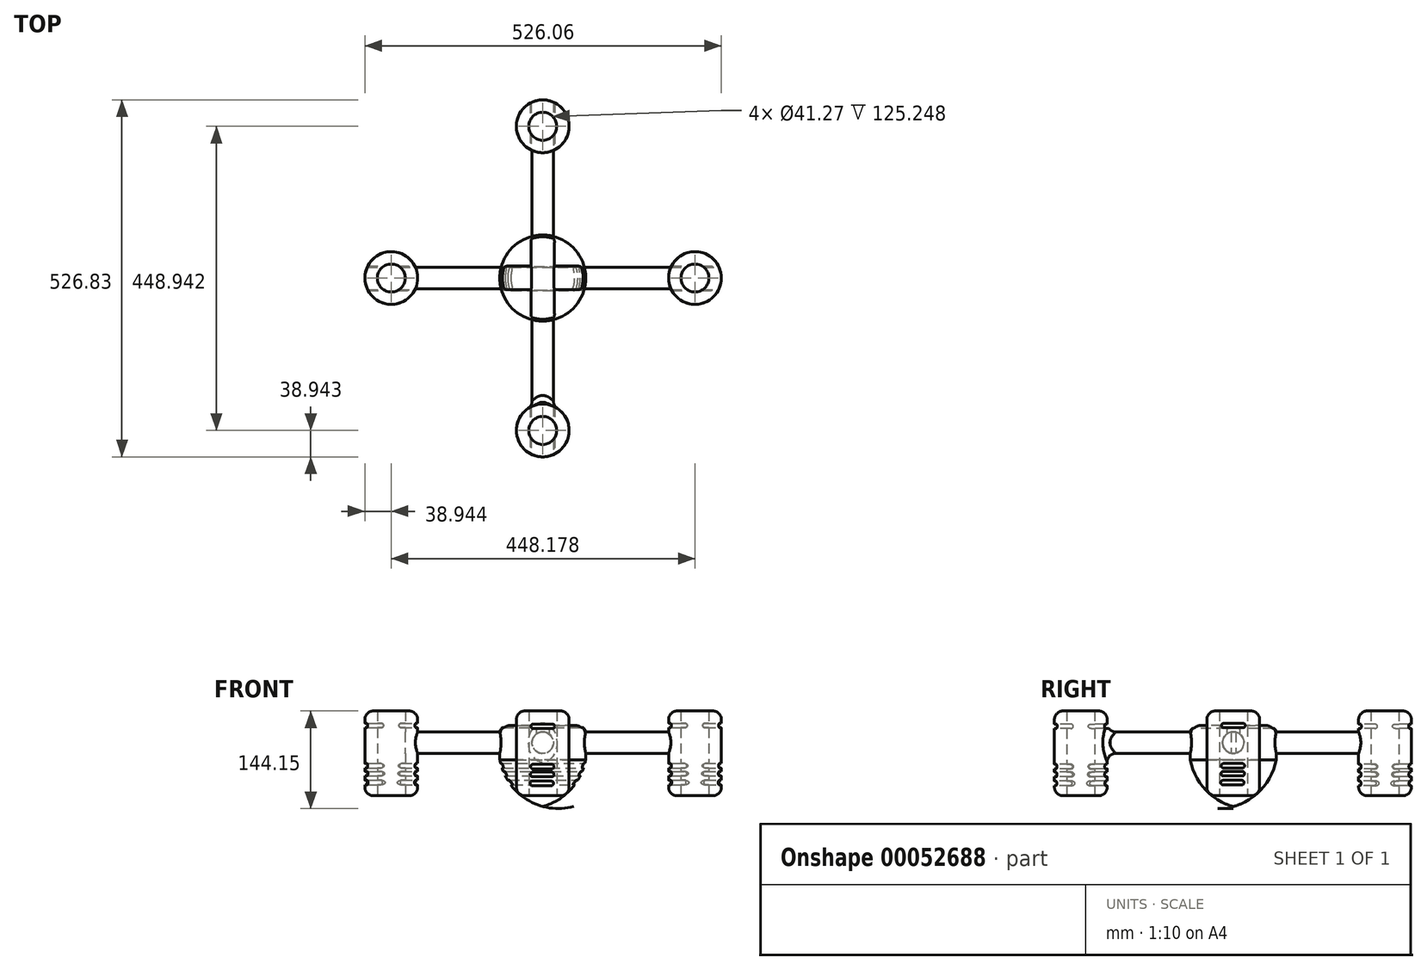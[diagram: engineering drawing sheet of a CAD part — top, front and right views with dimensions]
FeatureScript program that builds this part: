
annotation { "Feature Type Name" : "Feature", "Feature Type Description" : "" }
export const myFeature = defineFeature(function(context is Context, id is Id, definition is map)
    precondition{}
    {
        {
            var Q0;
            Q0=qCreatedBy(makeId("Top.planeOp"),FACE);
            var sketch = newSketch(context, id + "F0", { "sketchPlane" : qUnion([Q0])});
            skCircle(sketch, "E0", {"center": v(0, 0) * mm, "radius": 63.5 * mm});
            skSolve(sketch);
        }
        {
            var Q0;
            Q0 = qSketchRegion(id + "F0", true);
            extrude(context, id + "F1", {"entities" : qUnion([Q0]), "depth" : 25.4 * mm, "hasSecondDirection" : true, "secondDirectionOppositeDirection" : true, "secondDirectionDepth" : 25.4 * mm});
        }
        {
            var Q0;
            Q0=qCreatedBy(makeId("Right.planeOp"),FACE);
            var sketch = newSketch(context, id + "F2", { "sketchPlane" : qUnion([Q0])});
            skCircle(sketch, "E1", {"center": v(0, 0) * mm, "radius": 15.88 * mm});
            skSolve(sketch);
        }
        {
            var Q0;
            Q0 = qSketchRegion(id + "F2", true);
            extrude(context, id + "F3", {"entities" : qUnion([Q0]), "operationType" : NewBodyOperationType.ADD, "depth" : 203.2 * mm, "hasSecondDirection" : true, "secondDirectionOppositeDirection" : true, "secondDirectionDepth" : 203.2 * mm});
        }
        {
            var Q0;
            Q0=qCreatedBy(makeId("Front.planeOp"),FACE);
            var sketch = newSketch(context, id + "F4", { "sketchPlane" : qUnion([Q0])});
            skCircle(sketch, "E2", {"center": v(0, 0) * mm, "radius": 15.88 * mm});
            skSolve(sketch);
        }
        {
            var Q0;
            Q0 = qSketchRegion(id + "F4", true);
            extrude(context, id + "F5", {"entities" : qUnion([Q0]), "operationType" : NewBodyOperationType.ADD, "depth" : 203.2 * mm, "hasSecondDirection" : true, "secondDirectionOppositeDirection" : true, "secondDirectionDepth" : 203.2 * mm});
        }
        {
            var Q0;
            Q0=qCreatedBy(makeId("Top.planeOp"),FACE);
            var sketch = newSketch(context, id + "F6", { "sketchPlane" : qUnion([Q0])});
            skCircle(sketch, "E3", {"center": v(0, 223.94) * mm, "radius": 20.64 * mm});
            skCircle(sketch, "E4", {"center": v(0, 223.94) * mm, "radius": 38.94 * mm});
            skCircle(sketch, "E5", {"center": v(-223.55, 0) * mm, "radius": 20.64 * mm});
            skCircle(sketch, "E6", {"center": v(-223.55, 0) * mm, "radius": 38.94 * mm});
            skCircle(sketch, "E7", {"center": v(0, -225) * mm, "radius": 20.64 * mm});
            skCircle(sketch, "E8", {"center": v(0, -225) * mm, "radius": 38.94 * mm});
            skCircle(sketch, "E9", {"center": v(224.63, 0) * mm, "radius": 20.64 * mm});
            skCircle(sketch, "E10", {"center": v(224.63, 0) * mm, "radius": 38.94 * mm});
            skSolve(sketch);
        }
        {
            var Q0;
            Q0 = qSketchRegion(id + "F6", true);
            extrude(context, id + "F7", {"entities" : qUnion([Q0]), "operationType" : NewBodyOperationType.ADD, "depth" : 46.84 * mm, "hasSecondDirection" : true, "secondDirectionOppositeDirection" : true, "secondDirectionDepth" : 78.4 * mm});
        }
        {
            var Q0;
            Q0=makeQuery(id+"F1.opExtrude","CAP_EDGE",EDGE,{"disambiguationData":[OSD([sQuery(id+"F0.wireOp",EDGE,"E0")])],"isStart":false});
            var Q1;
            {var subQ0=sQuery(id+"F4.wireOp",EDGE,"E2");Q1=makeQuery(id+"F7.boolean.opBoolean","INTERSECT",EDGE,{"derivedFrom":[makeQuery(id+"F5.boolean.opBoolean","SPLIT",FACE,{"disambiguationData":[TD([makeQuery(id+"F5.opExtrude","CAP_FACE",FACE,{"disambiguationData":[OSD([subQ0])],"isStart":false})])],"derivedFrom":makeQuery(id+"F5.opExtrude","SWEPT_FACE",FACE,{"disambiguationData":[OSD([subQ0])]})}),makeQuery(id+"F7.opExtrude","SWEPT_FACE",FACE,{"disambiguationData":[OSD([sQuery(id+"F6.wireOp",EDGE,"E8")])]})]});}
            var Q2;
            Q2=makeQuery(id+"F7.opExtrude","CAP_EDGE",EDGE,{"disambiguationData":[OSD([sQuery(id+"F6.wireOp",EDGE,"E10")])],"isStart":false});
            var Q3;
            Q3=makeQuery(id+"F7.opExtrude","CAP_EDGE",EDGE,{"disambiguationData":[OSD([sQuery(id+"F6.wireOp",EDGE,"E10")])],"isStart":true});
            var Q4;
            Q4=makeQuery(id+"F7.opExtrude","CAP_EDGE",EDGE,{"disambiguationData":[OSD([sQuery(id+"F6.wireOp",EDGE,"E4")])],"isStart":true});
            var Q5;
            Q5=makeQuery(id+"F7.opExtrude","CAP_EDGE",EDGE,{"disambiguationData":[OSD([sQuery(id+"F6.wireOp",EDGE,"E4")])],"isStart":false});
            var Q6;
            Q6=makeQuery(id+"F7.opExtrude","CAP_EDGE",EDGE,{"disambiguationData":[OSD([sQuery(id+"F6.wireOp",EDGE,"E6")])],"isStart":false});
            var Q7;
            Q7=makeQuery(id+"F7.opExtrude","CAP_EDGE",EDGE,{"disambiguationData":[OSD([sQuery(id+"F6.wireOp",EDGE,"E6")])],"isStart":true});
            var Q8;
            Q8=makeQuery(id+"F7.opExtrude","CAP_EDGE",EDGE,{"disambiguationData":[OSD([sQuery(id+"F6.wireOp",EDGE,"E8")])],"isStart":false});
            var Q9;
            Q9=makeQuery(id+"F7.opExtrude","CAP_EDGE",EDGE,{"disambiguationData":[OSD([sQuery(id+"F6.wireOp",EDGE,"E8")])],"isStart":true});
            fillet(context, id + "F8", {"entities" : qUnion([Q0, Q1, Q2, Q3, Q4, Q5, Q6, Q7, Q8, Q9]), "radius" : 12.7 * mm, "tangentPropagation" : true, "allowEdgeOverflow" : false});
        }
        {
            var Q0;
            Q0=qCreatedBy(makeId("Front.planeOp"),FACE);
            var sketch = newSketch(context, id + "F9", { "sketchPlane" : qUnion([Q0])});
            skLineSegment(sketch, "E11.rect.bottom", {"start": v(-14, 20.7) * mm, "end": v(14, 20.7) * mm});
            skLineSegment(sketch, "E11.rect.top", {"start": v(-14, 27.53) * mm, "end": v(14, 27.53) * mm});
            skPoint(sketch, "E11.rect.middle", {"position": v(0, 24.12) * mm});
            skArc(sketch, "E12", {"start": v(-14, 27.53) * mm, "mid": v(-17.4, 24.12) * mm, "end": v(-14, 20.7) * mm});
            skArc(sketch, "E13", {"start": v(14, 20.7) * mm, "mid": v(17.4, 24.12) * mm, "end": v(14, 27.53) * mm});
            skLineSegment(sketch, "E14.rect.bottom", {"start": v(-15.35, -63.59) * mm, "end": v(12.4, -63.59) * mm});
            skLineSegment(sketch, "E14.rect.top", {"start": v(-15.35, -56.77) * mm, "end": v(12.4, -56.77) * mm});
            skArc(sketch, "E15", {"start": v(-15.35, -56.77) * mm, "mid": v(-18.76, -60.18) * mm, "end": v(-15.35, -63.59) * mm});
            skArc(sketch, "E16", {"start": v(12.4, -63.59) * mm, "mid": v(15.8, -60.18) * mm, "end": v(12.4, -56.77) * mm});
            skPoint(sketch, "E14.rect.middle", {"position": v(-1.48, -60.18) * mm});
            skLineSegment(sketch, "E17.rect.bottom", {"start": v(-14.37, -38.8) * mm, "end": v(13.19, -38.8) * mm});
            skArc(sketch, "E18", {"start": v(-14.37, -31.98) * mm, "mid": v(-17.78, -35.39) * mm, "end": v(-14.37, -38.8) * mm});
            skLineSegment(sketch, "E17.rect.top", {"start": v(-14.37, -31.98) * mm, "end": v(13.19, -31.98) * mm});
            skLineSegment(sketch, "E19.rect.bottom", {"start": v(-14.86, -50.33) * mm, "end": v(13.16, -50.33) * mm});
            skPoint(sketch, "E19.rect.middle", {"position": v(-0.85, -46.92) * mm});
            skPoint(sketch, "E17.rect.middle", {"position": v(-0.6, -35.39) * mm});
            skLineSegment(sketch, "E19.rect.top", {"start": v(-14.86, -43.51) * mm, "end": v(13.16, -43.51) * mm});
            skArc(sketch, "E20", {"start": v(-14.86, -43.51) * mm, "mid": v(-18.27, -46.92) * mm, "end": v(-14.86, -50.33) * mm});
            skArc(sketch, "E21", {"start": v(13.16, -50.33) * mm, "mid": v(16.57, -46.92) * mm, "end": v(13.16, -43.51) * mm});
            skArc(sketch, "E22", {"start": v(13.19, -38.8) * mm, "mid": v(16.6, -35.39) * mm, "end": v(13.19, -31.98) * mm});
            skSolve(sketch);
        }
        {
            var Q0;
            Q0 = qSketchRegion(id + "F9", true);
            extrude(context, id + "F10", {"entities" : qUnion([Q0]), "operationType" : NewBodyOperationType.REMOVE, "oppositeDirection" : true, "depth" : 285.84 * mm, "hasSecondDirection" : true, "secondDirectionOppositeDirection" : false, "secondDirectionDepth" : 295.64 * mm});
        }
        {
            var Q0;
            Q0=qCreatedBy(makeId("Front.planeOp"),FACE);
            var sketch = newSketch(context, id + "F11", { "sketchPlane" : qUnion([Q0])});
            skLineSegment(sketch, "E23", {"start": v(0, -25.3) * mm, "end": v(0, -94.25) * mm});
            skLineSegment(sketch, "E24", {"start": v(0, -25.3) * mm, "end": v(63.29, -25.3) * mm});
            skArc(sketch, "E25", {"start": v(0, -94.25) * mm, "mid": v(41.62, -68.93) * mm, "end": v(63.29, -25.3) * mm});
            skSolve(sketch);
        }
        {
            var Q0;
            Q0 = qSketchRegion(id + "F11", true);
            var Q1;
            Q1=sQuery(id+"F11.wireOp",EDGE,"E23");
            revolve(context, id + "F12", {"operationType" : NewBodyOperationType.ADD, "entities" : qUnion([Q0]), "axis" : qUnion([Q1]), "revolveType" : RevolveType.FULL});
        }
        {
            var Q0;
            Q0=qCreatedBy(makeId("Right.planeOp"),FACE);
            var sketch = newSketch(context, id + "F13", { "sketchPlane" : qUnion([Q0])});
            skLineSegment(sketch, "E26.rect.bottom", {"start": v(-13.79, 21.92) * mm, "end": v(14.21, 21.92) * mm});
            skLineSegment(sketch, "E26.rect.top", {"start": v(-13.79, 28.73) * mm, "end": v(14.21, 28.73) * mm});
            skPoint(sketch, "E26.rect.middle", {"position": v(0.21, 25.33) * mm});
            skArc(sketch, "E27", {"start": v(-13.79, 28.73) * mm, "mid": v(-17.2, 25.33) * mm, "end": v(-13.79, 21.92) * mm});
            skArc(sketch, "E28", {"start": v(14.21, 21.92) * mm, "mid": v(17.62, 25.33) * mm, "end": v(14.21, 28.73) * mm});
            skLineSegment(sketch, "E29.rect.bottom", {"start": v(-15.14, -62.38) * mm, "end": v(12.61, -62.38) * mm});
            skLineSegment(sketch, "E29.rect.top", {"start": v(-15.14, -55.56) * mm, "end": v(12.61, -55.56) * mm});
            skArc(sketch, "E30", {"start": v(-15.14, -55.56) * mm, "mid": v(-18.55, -58.97) * mm, "end": v(-15.14, -62.38) * mm});
            skArc(sketch, "E31", {"start": v(12.61, -62.38) * mm, "mid": v(16.02, -58.97) * mm, "end": v(12.61, -55.56) * mm});
            skPoint(sketch, "E29.rect.middle", {"position": v(-1.26, -58.97) * mm});
            skLineSegment(sketch, "E32.rect.bottom", {"start": v(-14.16, -37.59) * mm, "end": v(13.4, -37.59) * mm});
            skArc(sketch, "E33", {"start": v(-14.16, -30.77) * mm, "mid": v(-17.57, -34.18) * mm, "end": v(-14.16, -37.59) * mm});
            skLineSegment(sketch, "E32.rect.top", {"start": v(-14.16, -30.77) * mm, "end": v(13.4, -30.77) * mm});
            skLineSegment(sketch, "E34.rect.bottom", {"start": v(-14.65, -49.12) * mm, "end": v(13.37, -49.12) * mm});
            skPoint(sketch, "E34.rect.middle", {"position": v(-0.64, -45.71) * mm});
            skPoint(sketch, "E32.rect.middle", {"position": v(-0.38, -34.18) * mm});
            skLineSegment(sketch, "E34.rect.top", {"start": v(-14.65, -42.3) * mm, "end": v(13.37, -42.3) * mm});
            skArc(sketch, "E35", {"start": v(-14.65, -42.3) * mm, "mid": v(-18.06, -45.71) * mm, "end": v(-14.65, -49.12) * mm});
            skArc(sketch, "E36", {"start": v(13.37, -49.12) * mm, "mid": v(16.78, -45.71) * mm, "end": v(13.37, -42.3) * mm});
            skArc(sketch, "E37", {"start": v(13.4, -37.59) * mm, "mid": v(16.8, -34.18) * mm, "end": v(13.4, -30.77) * mm});
            skSolve(sketch);
        }
        {
            var Q0;
            Q0 = qSketchRegion(id + "F13", true);
            extrude(context, id + "F14", {"entities" : qUnion([Q0]), "operationType" : NewBodyOperationType.REMOVE, "oppositeDirection" : true, "depth" : 346.92 * mm, "hasSecondDirection" : true, "secondDirectionOppositeDirection" : false, "secondDirectionDepth" : 308.7 * mm});
        }
    });
